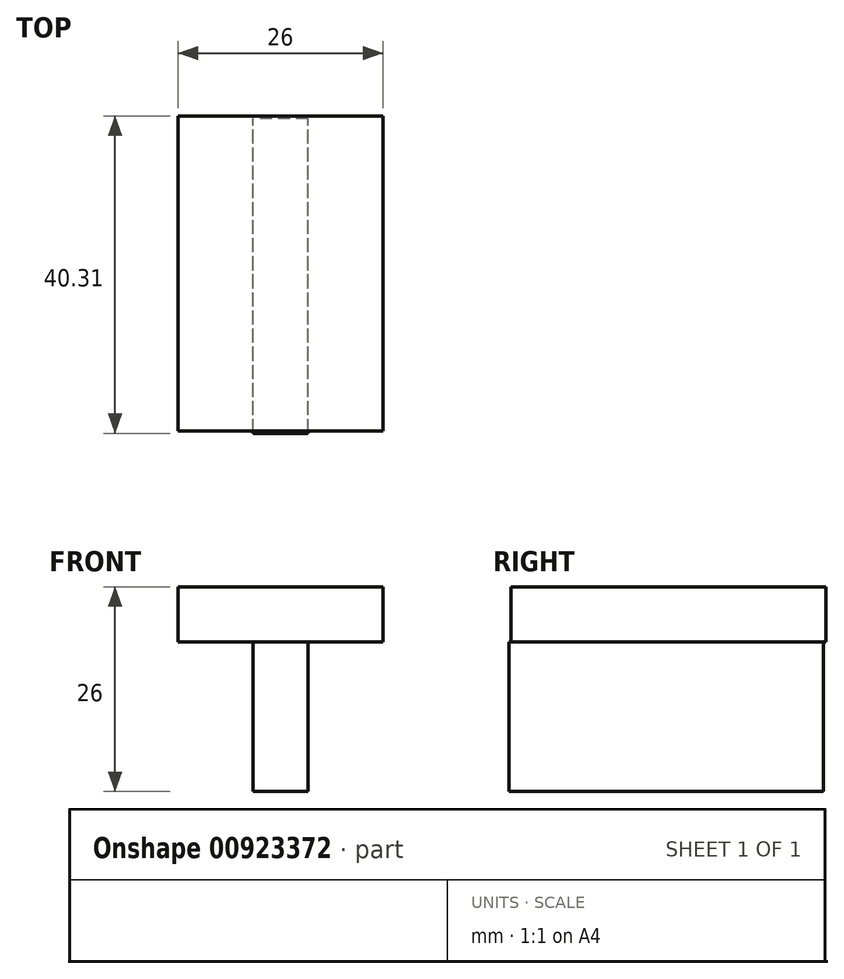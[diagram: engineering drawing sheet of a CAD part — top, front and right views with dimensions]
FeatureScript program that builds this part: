
annotation { "Feature Type Name" : "Feature", "Feature Type Description" : "" }
export const myFeature = defineFeature(function(context is Context, id is Id, definition is map)
    precondition{}
    {
        {
            var Q0;
            Q0=qCreatedBy(makeId("Right.planeOp"),FACE);
            var sketch = newSketch(context, id + "F0", { "sketchPlane" : qUnion([Q0])});
            skLineSegment(sketch, "E0.bottom", {"start": v(-20.3, 0) * mm, "end": v(19.7, 0) * mm});
            skLineSegment(sketch, "E0.top", {"start": v(-20.3, -19) * mm, "end": v(19.7, -19) * mm});
            skLineSegment(sketch, "E0.left", {"start": v(-20.3, 0) * mm, "end": v(-20.3, -19) * mm});
            skLineSegment(sketch, "E0.right", {"start": v(19.7, 0) * mm, "end": v(19.7, -19) * mm});
            skSolve(sketch);
        }
        {
            var Q0;
            Q0=qCreatedBy(makeId("Top.planeOp"),FACE);
            var sketch = newSketch(context, id + "F1", { "sketchPlane" : qUnion([Q0])});
            skLineSegment(sketch, "E1.bottom", {"start": v(13, -20) * mm, "end": v(-13, -20) * mm});
            skLineSegment(sketch, "E1.top", {"start": v(13, 20) * mm, "end": v(-13, 20) * mm});
            skLineSegment(sketch, "E1.left", {"start": v(13, -20) * mm, "end": v(13, 20) * mm});
            skLineSegment(sketch, "E1.right", {"start": v(-13, -20) * mm, "end": v(-13, 20) * mm});
            skPoint(sketch, "E1.middle", {"position": v(0, 0) * mm});
            skSolve(sketch);
        }
        {
            var Q0;
            Q0 = qSketchRegion(id + "F1", true);
            extrude(context, id + "F2", {"entities" : qUnion([Q0]), "depth" : 7 * mm, "offsetDistance" : 25 * mm});
        }
        {
            var Q0;
            Q0 = qSketchRegion(id + "F0", true);
            extrude(context, id + "F3", {"entities" : qUnion([Q0]), "operationType" : NewBodyOperationType.ADD, "depth" : 7 * mm, "offsetDistance" : 25 * mm, "symmetric" : true});
        }
    });
